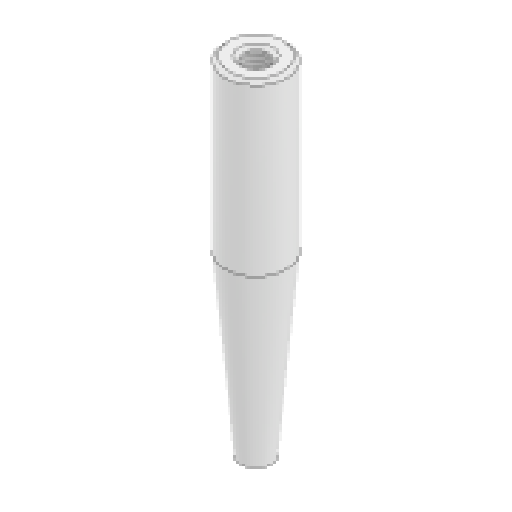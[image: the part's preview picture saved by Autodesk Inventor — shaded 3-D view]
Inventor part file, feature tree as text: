
AUTODESK INVENTOR PART (.ipt)
format: ipt  version: 2025.2 (Build 292293000, 293)  size: 118,272 bytes
history: native  units: in
note: dims shown in document units (in); Inventor stores cm internally (conversion verified against a paired STEP export)
features: sketch x2, revolve x1, hole x1, chamfer x1
ambient origin geometry x8: Origin, YZ Plane, XZ Plane, XY Plane, X Axis, Y Axis, Z Axis, Center Point
bodies: Solid1 (feature_tree)
feature tree (5):
  revolve  "Revolution1"  [1 undecoded]
  hole  "Hole1"  [1 undecoded]
  chamfer  "Chamfer1"  Distance=1.7717in
  sketch  "Sketch1"  dims[d2=0.315in d5=0.9055in]
  sketch  "Sketch2"  dims[d7=360.0deg d10=0.0197in d11=0.0787in d12=45.0deg d14=0.1276in d15=0.7874in d16=0.3937in d17=0.0787in d18=90.0deg d19=0.9843in d20=0.8108in d21=1.7717in d22=0.1565in d23=0.0344in]
note: 2 required parameter values undecoded (feature->parameter linkage not recoverable at this tier; creation-order binding heuristic only, values carry confidence <= 0.55)